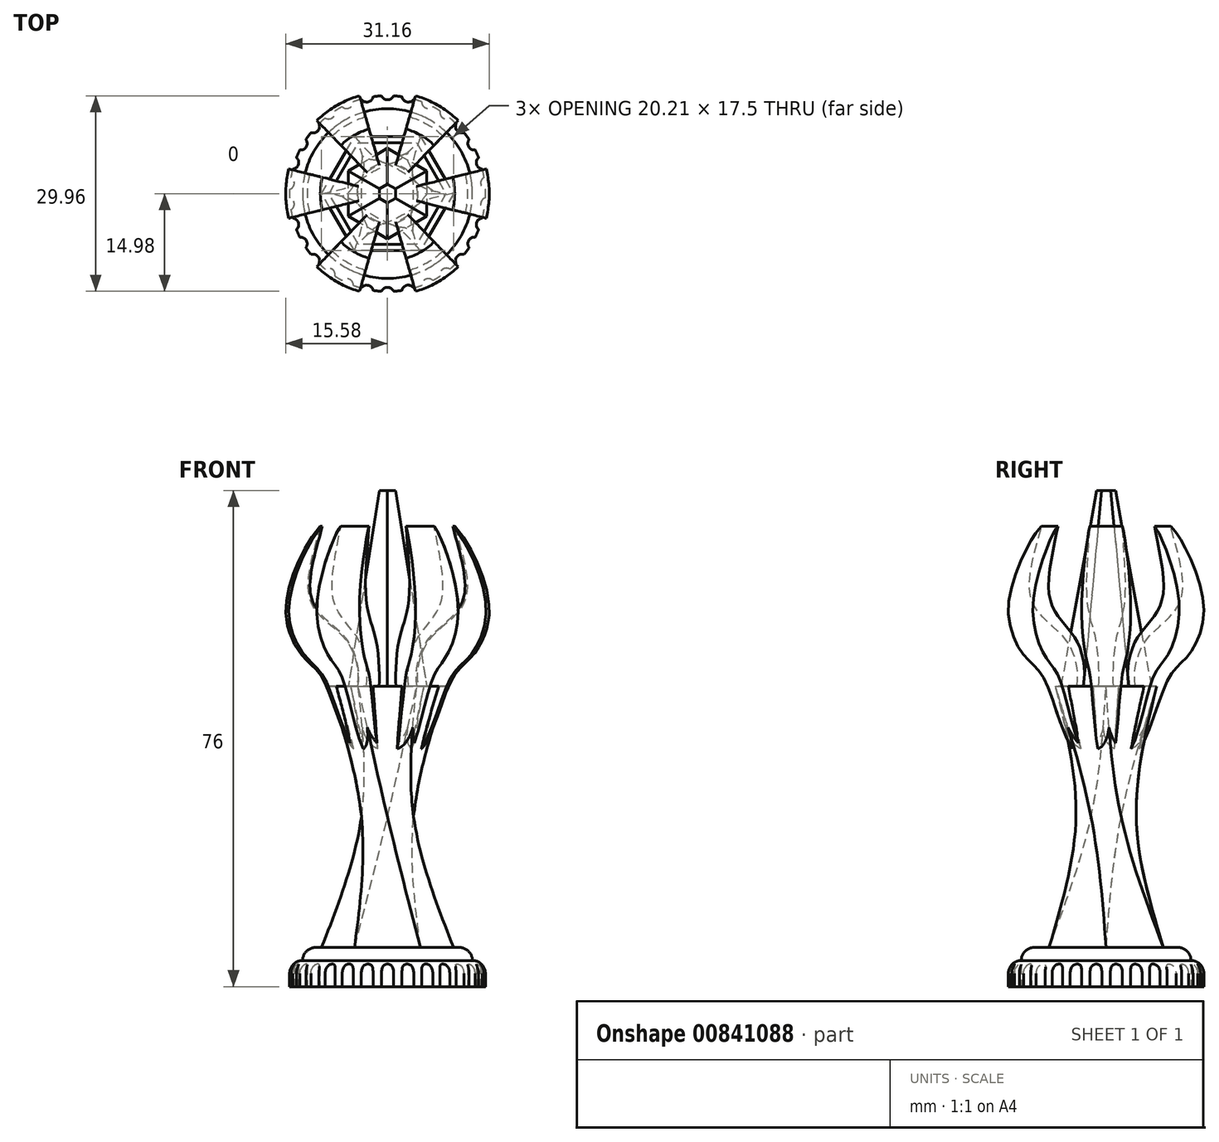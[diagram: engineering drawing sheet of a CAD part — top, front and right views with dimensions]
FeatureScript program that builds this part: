
annotation { "Feature Type Name" : "Feature", "Feature Type Description" : "" }
export const myFeature = defineFeature(function(context is Context, id is Id, definition is map)
    precondition{}
    {
        {
            var Q0;
            Q0=qCreatedBy(makeId("Top.planeOp"),FACE);
            var sketch = newSketch(context, id + "F0", { "sketchPlane" : qUnion([Q0])});
            skCircle(sketch, "E0", {"center": v(0, 0) * mm, "radius": 15 * mm});
            skSolve(sketch);
        }
        {
            var Q0;
            Q0 = qSketchRegion(id + "F0", true);
            extrude(context, id + "F1", {"entities" : qUnion([Q0]), "depth" : 4 * mm, "offsetDistance" : 25 * mm});
        }
        {
            var Q0;
            Q0=makeQuery(id+"F1.opExtrude","CAP_FACE",FACE,{"disambiguationData":[OSD([sQuery(id+"F0.wireOp",EDGE,"E0")])],"isStart":false});
            var sketch = newSketch(context, id + "F2", { "sketchPlane" : qUnion([Q0])});
            skCircle(sketch, "E1", {"center": v(0, 0) * mm, "radius": 13 * mm});
            skSolve(sketch);
        }
        {
            var Q0;
            Q0 = qSketchRegion(id + "F2", true);
            extrude(context, id + "F3", {"entities" : qUnion([Q0]), "operationType" : NewBodyOperationType.ADD, "depth" : 2 * mm, "offsetDistance" : 25 * mm});
        }
        {
            var Q0;
            Q0=makeQuery(id+"F1.opExtrude","CAP_EDGE",EDGE,{"disambiguationData":[OSD([sQuery(id+"F0.wireOp",EDGE,"E0")])],"isStart":false});
            var Q1;
            Q1=makeQuery(id+"F3.opExtrude","CAP_EDGE",EDGE,{"disambiguationData":[OSD([sQuery(id+"F2.wireOp",EDGE,"E1")])],"isStart":false});
            fillet(context, id + "F4", {"entities" : qUnion([Q0, Q1]), "radius" : 2 * mm, "tangentPropagation" : true, "allowEdgeOverflow" : false});
        }
        {
            var Q0;
            Q0=makeQuery(id+"F1.opExtrude","CAP_FACE",FACE,{"disambiguationData":[OSD([sQuery(id+"F0.wireOp",EDGE,"E0")])],"isStart":true});
            var sketch = newSketch(context, id + "F5", { "sketchPlane" : qUnion([Q0])});
            skCircle(sketch, "E2", {"center": v(0, 15.36) * mm, "radius": 1 * mm});
            skCircle(sketch, "E3.1.0", {"center": v(-3.2, 15.02) * mm, "radius": 1 * mm});
            skCircle(sketch, "E3.2.0", {"center": v(-6.25, 14.03) * mm, "radius": 1 * mm});
            skCircle(sketch, "E3.3.0", {"center": v(-9.03, 12.43) * mm, "radius": 1 * mm});
            skCircle(sketch, "E3.4.0", {"center": v(-11.41, 10.28) * mm, "radius": 1 * mm});
            skCircle(sketch, "E3.5.0", {"center": v(-13.3, 7.68) * mm, "radius": 1 * mm});
            skCircle(sketch, "E3.6.0", {"center": v(-14.6, 4.75) * mm, "radius": 1 * mm});
            skCircle(sketch, "E3.7.0", {"center": v(-15.27, 1.6) * mm, "radius": 1 * mm});
            skCircle(sketch, "E3.8.0", {"center": v(-15.27, -1.6) * mm, "radius": 1 * mm});
            skCircle(sketch, "E3.9.0", {"center": v(-14.6, -4.75) * mm, "radius": 1 * mm});
            skCircle(sketch, "E3.10.0", {"center": v(-13.3, -7.68) * mm, "radius": 1 * mm});
            skCircle(sketch, "E3.11.0", {"center": v(-11.41, -10.28) * mm, "radius": 1 * mm});
            skCircle(sketch, "E3.12.0", {"center": v(-9.03, -12.43) * mm, "radius": 1 * mm});
            skCircle(sketch, "E3.13.0", {"center": v(-6.25, -14.03) * mm, "radius": 1 * mm});
            skCircle(sketch, "E3.14.0", {"center": v(-3.2, -15.02) * mm, "radius": 1 * mm});
            skCircle(sketch, "E3.15.0", {"center": v(0, -15.36) * mm, "radius": 1 * mm});
            skCircle(sketch, "E3.16.0", {"center": v(3.2, -15.02) * mm, "radius": 1 * mm});
            skCircle(sketch, "E3.17.0", {"center": v(6.25, -14.03) * mm, "radius": 1 * mm});
            skCircle(sketch, "E3.18.0", {"center": v(9.03, -12.43) * mm, "radius": 1 * mm});
            skCircle(sketch, "E3.19.0", {"center": v(11.41, -10.28) * mm, "radius": 1 * mm});
            skCircle(sketch, "E3.20.0", {"center": v(13.3, -7.68) * mm, "radius": 1 * mm});
            skCircle(sketch, "E3.21.0", {"center": v(14.6, -4.75) * mm, "radius": 1 * mm});
            skCircle(sketch, "E3.22.0", {"center": v(15.27, -1.6) * mm, "radius": 1 * mm});
            skCircle(sketch, "E3.23.0", {"center": v(15.27, 1.6) * mm, "radius": 1 * mm});
            skCircle(sketch, "E3.24.0", {"center": v(14.6, 4.75) * mm, "radius": 1 * mm});
            skCircle(sketch, "E3.25.0", {"center": v(13.3, 7.68) * mm, "radius": 1 * mm});
            skCircle(sketch, "E3.26.0", {"center": v(11.41, 10.28) * mm, "radius": 1 * mm});
            skCircle(sketch, "E3.27.0", {"center": v(9.03, 12.43) * mm, "radius": 1 * mm});
            skCircle(sketch, "E3.28.0", {"center": v(6.25, 14.03) * mm, "radius": 1 * mm});
            skCircle(sketch, "E3.29.0", {"center": v(3.2, 15.02) * mm, "radius": 1 * mm});
            skPoint(sketch, "E3.center", {"position": v(0, 0) * mm});
            skSolve(sketch);
        }
        {
            var Q0;
            Q0 = qSketchRegion(id + "F5", true);
            extrude(context, id + "F6", {"entities" : qUnion([Q0]), "operationType" : NewBodyOperationType.REMOVE, "oppositeDirection" : true, "depth" : 25 * mm, "offsetDistance" : 25 * mm});
        }
        {
            var Q0;
            Q0=makeQuery(id+"F3.opExtrude","CAP_FACE",FACE,{"disambiguationData":[OSD([sQuery(id+"F2.wireOp",EDGE,"E1")])],"isStart":false});
            var sketch = newSketch(context, id + "F7", { "sketchPlane" : qUnion([Q0])});
            skCircle(sketch, "E4.cCircle", {"center": v(0, 0) * mm, "radius": 8.75 * mm, "construction": true});
            skLineSegment(sketch, "E4.0", {"start": v(10.1, 0) * mm, "end": v(5.05, -8.75) * mm});
            skLineSegment(sketch, "E4.1", {"start": v(5.05, -8.75) * mm, "end": v(-5.05, -8.75) * mm});
            skLineSegment(sketch, "E4.2", {"start": v(-5.05, -8.75) * mm, "end": v(-10.1, 0) * mm});
            skLineSegment(sketch, "E4.3", {"start": v(-10.1, 0) * mm, "end": v(-5.05, 8.75) * mm});
            skLineSegment(sketch, "E4.4", {"start": v(-5.05, 8.75) * mm, "end": v(5.05, 8.75) * mm});
            skLineSegment(sketch, "E4.5", {"start": v(5.05, 8.75) * mm, "end": v(10.1, 0) * mm});
            skPoint(sketch, "E4.0.midPoint", {"position": v(7.58, -4.38) * mm});
            skSolve(sketch);
        }
        {
            var Q0;
            Q0=makeQuery(id+"F7.imprint","IMPRINT",FACE,{"disambiguationData":[TD([[makeQuery(id+"F7.imprint","IMPRINT",EDGE,{"derivedFrom":sQuery(id+"F7.wireOp",EDGE,"E4.0")}),1.0]])]});
            cPlane(context, id + "F8", {"entities" : qUnion([Q0]), "cplaneType" : CPlaneType.OFFSET, "offset" : 20 * mm, "width" : 150 * mm, "height" : 150 * mm});
        }
        {
            var Q0;
            Q0=qCreatedBy(id+"F8.planeOp",FACE);
            cPlane(context, id + "F9", {"entities" : qUnion([Q0]), "cplaneType" : CPlaneType.OFFSET, "offset" : 20 * mm, "width" : 150 * mm, "height" : 150 * mm});
        }
        {
            var Q0;
            Q0=qCreatedBy(id+"F8.planeOp",FACE);
            var sketch = newSketch(context, id + "F10", { "sketchPlane" : qUnion([Q0])});
            skCircle(sketch, "E5.cCircle", {"center": v(0, 0) * mm, "radius": 4 * mm, "construction": true});
            skLineSegment(sketch, "E5.0", {"start": v(4, 2.3) * mm, "end": v(4, -2.3) * mm});
            skLineSegment(sketch, "E5.1", {"start": v(4, -2.3) * mm, "end": v(0, -4.62) * mm});
            skLineSegment(sketch, "E5.2", {"start": v(0, -4.62) * mm, "end": v(-4, -2.3) * mm});
            skLineSegment(sketch, "E5.3", {"start": v(-4, -2.3) * mm, "end": v(-4, 2.3) * mm});
            skLineSegment(sketch, "E5.4", {"start": v(-4, 2.3) * mm, "end": v(0, 4.62) * mm});
            skLineSegment(sketch, "E5.5", {"start": v(0, 4.62) * mm, "end": v(4, 2.3) * mm});
            skPoint(sketch, "E5.0.midPoint", {"position": v(4, 0) * mm});
            skSolve(sketch);
        }
        {
            var Q0;
            Q0=qCreatedBy(id+"F9.planeOp",FACE);
            var sketch = newSketch(context, id + "F11", { "sketchPlane" : qUnion([Q0])});
            skCircle(sketch, "E6.cCircle", {"center": v(0, 0) * mm, "radius": 7.75 * mm, "construction": true});
            skLineSegment(sketch, "E6.0", {"start": v(-4.47, 7.75) * mm, "end": v(4.47, 7.75) * mm});
            skLineSegment(sketch, "E6.1", {"start": v(4.47, 7.75) * mm, "end": v(8.95, 0) * mm});
            skLineSegment(sketch, "E6.2", {"start": v(8.95, 0) * mm, "end": v(4.47, -7.75) * mm});
            skLineSegment(sketch, "E6.3", {"start": v(4.47, -7.75) * mm, "end": v(-4.47, -7.75) * mm});
            skLineSegment(sketch, "E6.4", {"start": v(-4.47, -7.75) * mm, "end": v(-8.95, 0) * mm});
            skLineSegment(sketch, "E6.5", {"start": v(-8.95, 0) * mm, "end": v(-4.47, 7.75) * mm});
            skPoint(sketch, "E6.0.midPoint", {"position": v(0, 7.75) * mm});
            skSolve(sketch);
        }
        {
            var Q1;
            Q1=makeQuery(id+"F7.imprint","IMPRINT",FACE,{"disambiguationData":[TD([[makeQuery(id+"F7.imprint","IMPRINT",EDGE,{"derivedFrom":sQuery(id+"F7.wireOp",EDGE,"E4.0")}),-1.0]])]});
            var Q2;
            Q2=makeQuery(id+"F10.imprint","IMPRINT",FACE,{"disambiguationData":[TD([[makeQuery(id+"F10.imprint","IMPRINT",EDGE,{"derivedFrom":sQuery(id+"F10.wireOp",EDGE,"E5.0")}),-1.0]])]});
            var Q3;
            Q3=makeQuery(id+"F11.imprint","IMPRINT",FACE,{"disambiguationData":[TD([[makeQuery(id+"F11.imprint","IMPRINT",EDGE,{"derivedFrom":sQuery(id+"F11.wireOp",EDGE,"E6.0")}),-1.0]])]});
            var Q4;
            Q4=sQuery(id+"F7.wireOp",VERTEX,"E4.2.end");
            var Q5;
            Q5=sQuery(id+"F10.wireOp",VERTEX,"E5.3.end");
            var Q6;
            Q6=sQuery(id+"F11.wireOp",VERTEX,"E6.0.start");
            loft(context, id + "F12", {"operationType" : NewBodyOperationType.ADD, "sheetProfilesArray" : [{ "sheetProfileEntities" : qUnion([Q1]) }, { "sheetProfileEntities" : qUnion([Q2]) }, { "sheetProfileEntities" : qUnion([Q3]) }], "matchConnections" : true, "connections" : [{ "connectionEntities" : qUnion([Q4, Q5, Q6]), "connectionEdgeQueries" : qUnion([]), "connectionEdgeParameters" : [] }]});
        }
        {
            var Q0;
            Q0=qCreatedBy(makeId("Front.planeOp"),FACE);
            var sketch = newSketch(context, id + "F13", { "sketchPlane" : qUnion([Q0])});
            skLineSegment(sketch, "E7", {"start": v(0, 0) * mm, "end": v(0, 62.44) * mm, "construction": true});
            skSolve(sketch);
        }
        {
            var Q0;
            Q0=qCreatedBy(makeId("Front.planeOp"),FACE);
            var sketch = newSketch(context, id + "F14", { "sketchPlane" : qUnion([Q0])});
            skFitSpline(sketch, "E8", {"points": [v(-5.21, 36.26) * mm, v(-9.94, 47.2) * mm, v(-12.88, 50.53) * mm, v(-15.57, 58.12) * mm, v(-11.58, 68.95) * mm, v(-10.29, 70.55) * mm], "startDerivative": vector(-22.68, 30.74) * mm, "endDerivative": vector(9.32, 10.03) * mm});
            skFitSpline(sketch, "E9", {"points": [v(-5.21, 36.26) * mm, v(-5.06, 41.11) * mm, v(-5.21, 44.6) * mm], "startDerivative": vector(6.65, 6.53) * mm, "endDerivative": vector(1.42, 12.01) * mm});
            skFitSpline(sketch, "E10", {"points": [v(-5.21, 44.6) * mm, v(-4.54, 47.04) * mm, v(-5.79, 52.25) * mm, v(-9.46, 56) * mm, v(-12.2, 60.59) * mm, v(-10.29, 70.55) * mm], "startDerivative": vector(7.83, 14.65) * mm, "endDerivative": vector(7.48, 29.36) * mm});
            skSolve(sketch);
        }
        {
            var Q0;
            Q0 = qSketchRegion(id + "F14", true);
            var Q1;
            Q1=sQuery(id+"F13.wireOp",EDGE,"E7");
            revolve(context, id + "F15", {"operationType" : NewBodyOperationType.ADD, "surfaceOperationType" : NewSurfaceOperationType.NEW, "entities" : qUnion([Q0]), "axis" : qUnion([Q1]), "revolveType" : RevolveType.SYMMETRIC, "angle" : 28 * degree});
        }
        {
            var Q0;
            Q0=makeQuery(id+"F1.opExtrude","SWEPT_BODY",BODY,{"disambiguationData":[OSD([sQuery(id+"F0.wireOp",EDGE,"E0")])]});
            var Q1;
            Q1=sQuery(id+"F13.wireOp",EDGE,"E7");
            circularPattern(context, id + "F16", {"entities" : qUnion([Q0]), "axis" : qUnion([Q1]), "angle" : 360 * degree, "instanceCount" : 6, "equalSpace" : true});
        }
        {
            var Q0;
            Q0=makeQuery(id+"F11.imprint","IMPRINT",FACE,{"disambiguationData":[TD([[makeQuery(id+"F11.imprint","IMPRINT",EDGE,{"derivedFrom":sQuery(id+"F11.wireOp",EDGE,"E6.0")}),-1.0]])]});
            var sketch = newSketch(context, id + "F17", { "sketchPlane" : qUnion([Q0])});
            skCircle(sketch, "E11.cCircle", {"center": v(0, 0) * mm, "radius": 6 * mm, "construction": true});
            skLineSegment(sketch, "E11.0", {"start": v(6, 3.46) * mm, "end": v(6, -3.46) * mm});
            skLineSegment(sketch, "E11.1", {"start": v(6, -3.46) * mm, "end": v(0, -6.93) * mm});
            skLineSegment(sketch, "E11.2", {"start": v(0, -6.93) * mm, "end": v(-6, -3.46) * mm});
            skLineSegment(sketch, "E11.3", {"start": v(-6, -3.46) * mm, "end": v(-6, 3.46) * mm});
            skLineSegment(sketch, "E11.4", {"start": v(-6, 3.46) * mm, "end": v(0, 6.93) * mm});
            skLineSegment(sketch, "E11.5", {"start": v(0, 6.93) * mm, "end": v(6, 3.46) * mm});
            skPoint(sketch, "E11.0.midPoint", {"position": v(6, 0) * mm});
            skSolve(sketch);
        }
        {
            var Q0;
            Q0=makeQuery(id+"F17.imprint","IMPRINT",FACE,{"disambiguationData":[TD([[makeQuery(id+"F17.imprint","IMPRINT",EDGE,{"derivedFrom":sQuery(id+"F17.wireOp",EDGE,"E11.0")}),-1.0]])]});
            extrude(context, id + "F18", {"entities" : qUnion([Q0]), "depth" : 30 * mm, "offsetDistance" : 25 * mm, "hasDraft" : true, "draftAngle" : 9 * degree, "draftPullDirection" : true});
        }
    });
